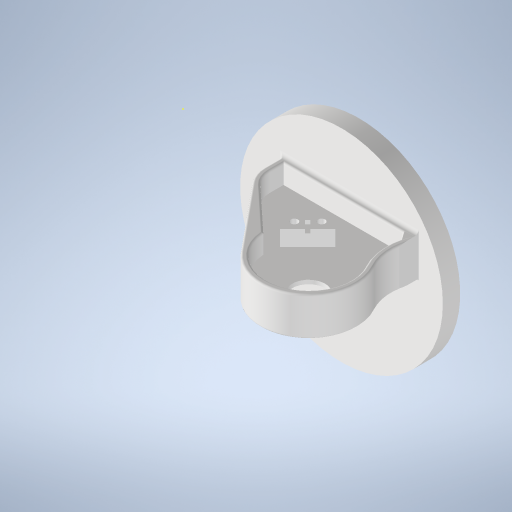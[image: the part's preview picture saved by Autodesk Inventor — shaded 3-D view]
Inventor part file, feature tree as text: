
AUTODESK INVENTOR PART (.ipt)
format: ipt  version: 2024.2 (Build 282272000, 272)  size: 1,221,120 bytes
history: native  units: mm
features: plane x10, extrude x9, fillet x8, other x8, projected_geometry x3, sketch x2, chamfer x2, reference x2, mirror x1
ambient origin geometry x8: Origin, YZ Plane, XZ Plane, XY Plane, X Axis, Y Axis, Z Axis, Center Point
bodies: Body1 (feature_tree)
feature tree (45):
  plane  "Work Plane1"
  extrude  "Extrusion2"  Depth=5.0mm TaperAngle=0.0deg
  plane  "Work Plane2"
  plane  "Work Plane3"
  plane  "Work Plane4"
  sketch  "Sketch5"  dims[d2=5.0mm d3=0.0mm d9=0.0mm d12=5.0mm]
  extrude  "Extrusion3"  Depth=10.0mm
  extrude  "Extrusion4"  Depth=10.0mm
  plane  "Work Plane5"
  extrude  "Extrusion5"  Depth=10.0mm
  chamfer  "Chamfer2"  Distance=10.5mm
  extrude  "Extrusion7"  TaperAngle=135.0deg  [1 undecoded]
  extrude  "Extrusion8"  Depth=10.0mm
  fillet  "Fillet1"  Radius=20.25mm
  extrude  "Extrusion9"  Depth=10.0mm
  fillet  "Fillet2"  Radius=20.25mm
  fillet  "Fillet3"  Radius=10.0mm
  fillet  "Fillet4"  Radius=10.0mm
  fillet  "Fillet5"  Radius=30.0mm
  plane  "Work Plane6"
  plane  "Work Plane9"
  fillet  "Fillet12"  Radius=50.0mm
  fillet  "Fillet13"  Radius=2.0mm
  plane  "Work Plane10"
  plane  "Work Plane11"
  extrude  "Extrusion13"  Depth=10.0mm
  plane  "Work Plane12"
  mirror  "Mirror7"
  chamfer  "Chamfer4"  Distance=10.0mm
  fillet  "Fillet14"  Radius=3.7mm
  extrude  "Extrusion14"  Depth=10.0mm
  reference  "Reference4"
  reference  "Reference5"
  projected_geometry  "Projected Loop2"
  projected_geometry  "Projected Loop4"
  projected_geometry  "Projected Loop5"
  sketch  "Sketch19"  dims[d13=30.0mm d14=40.0mm d16=21.0mm d17=38.0mm d26=10.5mm d27=135.0deg d28=9.5mm d30=20.25mm d31=40.25mm d32=20.25mm d33=10.0mm d34=10.0mm d35=30.0mm d37=50.0mm d39=2.0mm d40=0.0mm d41=50.0mm d43=10.0mm d44=0.0mm d45=3.7mm d46=3.7mm d47=6.3mm d48=3.0mm d49=3.0mm d51=20.5mm d52=6.0mm d53=0.0mm d62=2.0mm d63=2.0mm d64=45.0deg d65=30.0mm d66=15.0mm d67=10.0mm d68=10.0mm d69=0.0mm d70=5.0mm d71=8.0mm d73=5.0mm d74=7.5mm d75=0.0mm d76=0.0mm d77=2.0mm d81=20.0mm d82=0.0mm d86=2.0mm d87=1.0mm d88=1.0mm d89=1.0mm d96=20.5mm d97=5.245mm d111=1.0mm d112=1.0mm d114=21.25mm d115=20.125mm d116=17.0mm d119=1.0mm d120=1.0mm d121=15.0mm d138=4.88mm d147=4.0mm d148=1.0mm d149=1.0mm d150=2.0mm d151=0.0mm d152=21.0mm d153=2.0mm d154=1.0mm d155=2.0mm d156=4.0mm d157=2.0mm d158=45.0deg d159=1.0mm d160=5.0mm d161=4.0mm d162=0.0mm d163=3.5mm d113=0.5mm d122=0.872665mm d123=0.872665mm d124=0.5mm d125=0.872665mm]
  other  "<userpath> windows\Documents\Inventor\Robotska_roka\Assembly4.iam"
  other  "Assembly4.iam"
  other  "Servo Motor MG996R  With Attachments:2"
  other  "attachmentCircular_1"
  other  "podloga:1"
  other  "<userpath> windows\Documents\Inventor\Robotska_roka\roka.iam"
  other  "roka.iam"
  other  "roka1:1"
note: 1 required parameter value undecoded (feature->parameter linkage not recoverable at this tier; creation-order binding heuristic only, values carry confidence <= 0.55)
